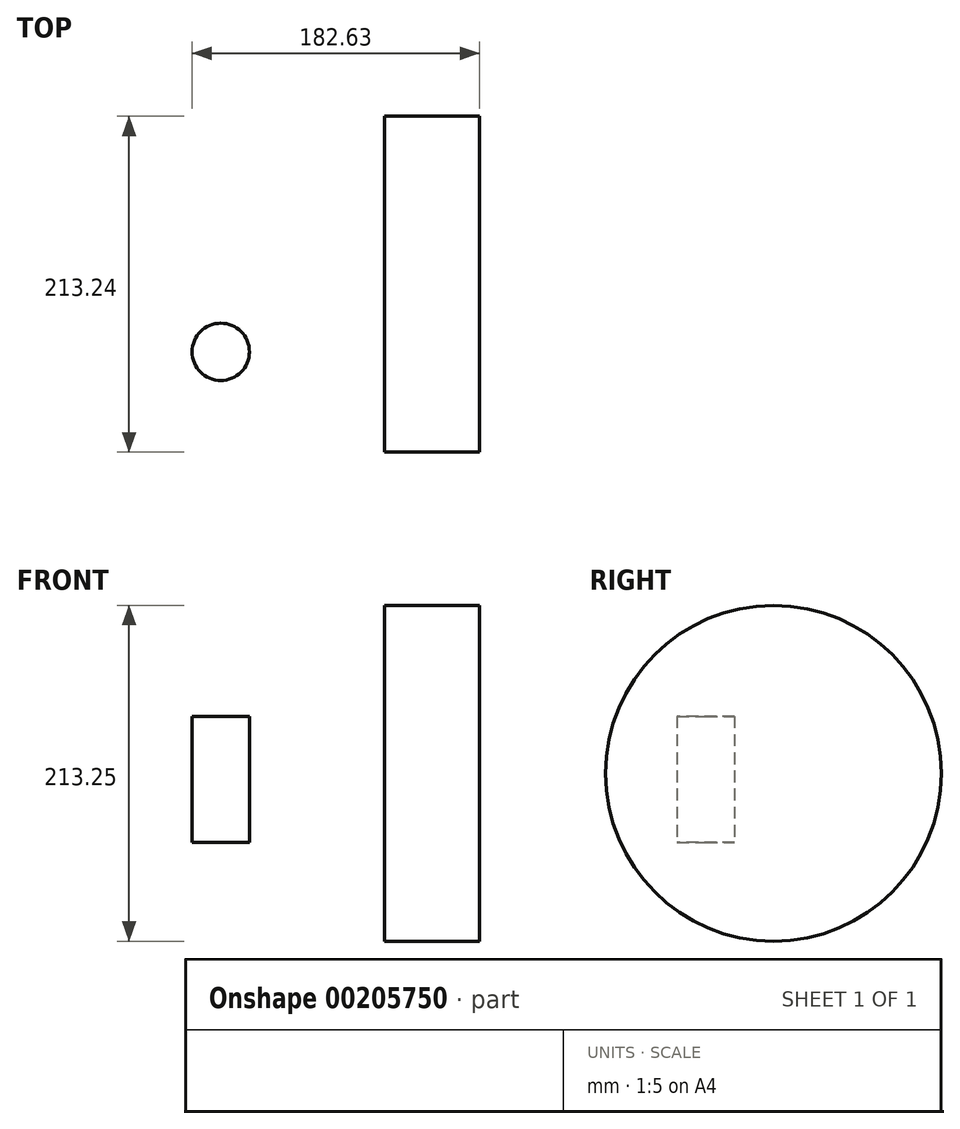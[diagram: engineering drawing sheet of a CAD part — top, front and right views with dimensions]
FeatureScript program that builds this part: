
annotation { "Feature Type Name" : "Feature", "Feature Type Description" : "" }
export const myFeature = defineFeature(function(context is Context, id is Id, definition is map)
    precondition{}
    {
        {
            var Q0;
            Q0=qCreatedBy(makeId("Top.planeOp"),FACE);
            var sketch = newSketch(context, id + "F0", { "sketchPlane" : qUnion([Q0])});
            skCircle(sketch, "E0", {"center": v(-133.15, -42.99) * mm, "radius": 18.2 * mm});
            skSolve(sketch);
        }
        {
            var Q0;
            Q0=makeQuery(id+"F0.imprint","IMPRINT",FACE,{"disambiguationData":[TD([[makeQuery(id+"F0.imprint","IMPRINT",EDGE,{"derivedFrom":sQuery(id+"F0.wireOp",EDGE,"E0")}),1.0]])]});
            extrude(context, id + "F1", {"entities" : qUnion([Q0]), "depth" : 80.26 * mm});
        }
        {
            var Q0;
            Q0=qCreatedBy(makeId("Front.planeOp"),FACE);
            var sketch = newSketch(context, id + "F2", { "sketchPlane" : qUnion([Q0])});
            skLineSegment(sketch, "E1.bottom", {"start": v(-29.2, 43.97) * mm, "end": v(31.28, 43.97) * mm});
            skLineSegment(sketch, "E1.top", {"start": v(-29.2, -62.66) * mm, "end": v(31.28, -62.66) * mm});
            skLineSegment(sketch, "E1.left", {"start": v(-29.2, 43.97) * mm, "end": v(-29.2, -62.66) * mm});
            skLineSegment(sketch, "E1.right", {"start": v(31.28, 43.97) * mm, "end": v(31.28, -62.66) * mm});
            skSolve(sketch);
        }
        {
            var Q0;
            Q0=makeQuery(id+"F2.imprint","IMPRINT",FACE,{"disambiguationData":[TD([[makeQuery(id+"F2.imprint","IMPRINT",EDGE,{"derivedFrom":sQuery(id+"F2.wireOp",EDGE,"E1.bottom")}),-1.0]])]});
            var Q1;
            Q1=sQuery(id+"F2.wireOp",EDGE,"E1.bottom");
            revolve(context, id + "F3", {"entities" : qUnion([Q0]), "axis" : qUnion([Q1]), "revolveType" : RevolveType.FULL});
        }
    });
